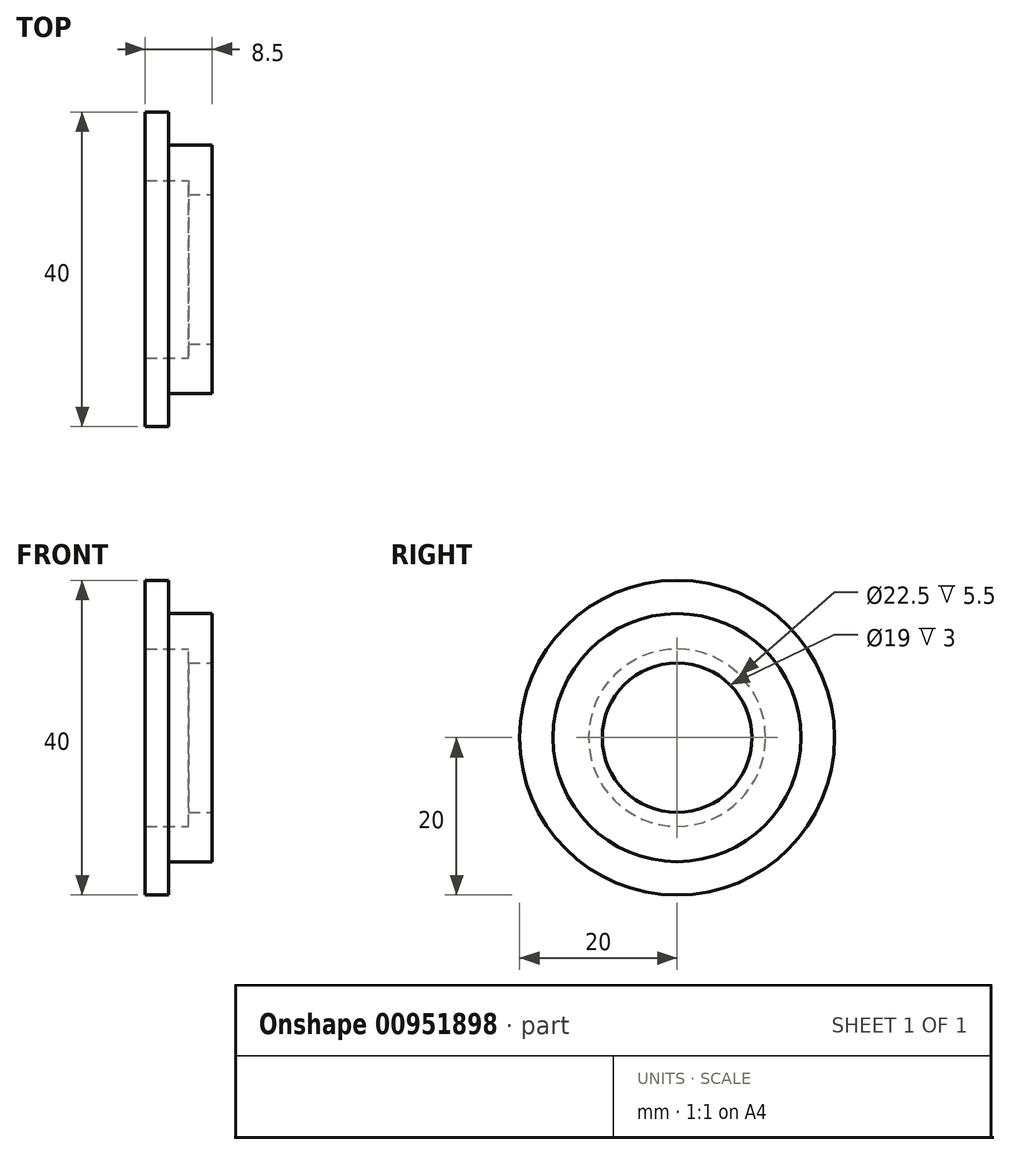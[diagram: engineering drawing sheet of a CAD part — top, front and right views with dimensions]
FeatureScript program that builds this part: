
annotation { "Feature Type Name" : "Feature", "Feature Type Description" : "" }
export const myFeature = defineFeature(function(context is Context, id is Id, definition is map)
    precondition{}
    {
        {
            var Q0;
            Q0=qCreatedBy(makeId("Top.planeOp"),FACE);
            var sketch = newSketch(context, id + "F0", { "sketchPlane" : qUnion([Q0])});
            skLineSegment(sketch, "E0", {"start": v(-3.83, 11.25) * mm, "end": v(-3.83, 20) * mm});
            skLineSegment(sketch, "E1", {"start": v(-3.83, 20) * mm, "end": v(-0.83, 20) * mm});
            skLineSegment(sketch, "E2", {"start": v(-0.83, 20) * mm, "end": v(-0.83, 15.75) * mm});
            skLineSegment(sketch, "E3", {"start": v(-0.83, 15.75) * mm, "end": v(4.67, 15.75) * mm});
            skLineSegment(sketch, "E4", {"start": v(4.67, 15.75) * mm, "end": v(4.67, 0) * mm});
            skLineSegment(sketch, "E5", {"start": v(4.67, 0) * mm, "end": v(1.67, 0) * mm});
            skLineSegment(sketch, "E6", {"start": v(-3.83, 11.25) * mm, "end": v(1.67, 11.25) * mm});
            skLineSegment(sketch, "E7", {"start": v(1.67, 11.25) * mm, "end": v(1.67, 0) * mm});
            skPoint(sketch, "E8.orphan", {"position": v(-3.83, 0) * mm});
            skSolve(sketch);
        }
        {
            var Q0;
            Q0=makeQuery(id+"F0.imprint","IMPRINT",FACE,{"disambiguationData":[TD([[makeQuery(id+"F0.imprint","IMPRINT",EDGE,{"derivedFrom":sQuery(id+"F0.wireOp",EDGE,"E0")}),-1.0]])]});
            var Q1;
            Q1=sQuery(id+"F0.wireOp",EDGE,"E5");
            revolve(context, id + "F1", {"surfaceOperationType" : NewSurfaceOperationType.NEW, "entities" : qUnion([Q0]), "axis" : qUnion([Q1]), "revolveType" : RevolveType.FULL});
        }
        {
            var Q0;
            Q0=makeQuery(id+"F1.opRevolve","SWEPT_FACE",FACE,{"disambiguationData":[OSD([sQuery(id+"F0.wireOp",EDGE,"E4")])]});
            var sketch = newSketch(context, id + "F2", { "sketchPlane" : qUnion([Q0])});
            skCircle(sketch, "E9", {"center": v(0, 0) * mm, "radius": 9.5 * mm});
            skSolve(sketch);
        }
        {
            var Q0;
            Q0=makeQuery(id+"F2.imprint","IMPRINT",FACE,{"disambiguationData":[TD([[makeQuery(id+"F2.imprint","IMPRINT",EDGE,{"derivedFrom":sQuery(id+"F2.wireOp",EDGE,"E9")}),1.0]])]});
            extrude(context, id + "F3", {"entities" : qUnion([Q0]), "operationType" : NewBodyOperationType.REMOVE, "oppositeDirection" : true, "depth" : 25 * mm, "offsetDistance" : 25 * mm});
        }
    });
